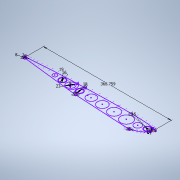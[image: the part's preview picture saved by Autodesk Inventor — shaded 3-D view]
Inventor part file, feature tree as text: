
AUTODESK INVENTOR PART (.ipt)
format: ipt  version: 2022 (Build 260153000, 153)  size: 203,264 bytes
history: native  units: mm
features: sketch x1
ambient origin geometry x8: Origin, YZ Plane, XZ Plane, XY Plane, X Axis, Y Axis, Z Axis, Center Point
feature tree (1):
  sketch  "Sketch1"  dims[d31=34.456mm d50=368.759386mm d57=16.0mm d69=8.0mm d70=23.0mm d71=8.0mm d73=16.0mm d80=19.0mm d81=16.0mm d82=1.0mm d83=1.0mm d84=1.0mm d85=1.0mm d86=1.0mm d87=0.8mm d88=1.0mm d90=19.0mm d94=5.0mm d95=5.0mm d101=5.0mm d102=5.0mm d105=5.0mm d106=5.0mm d108=2.0mm d109=19.0mm]
